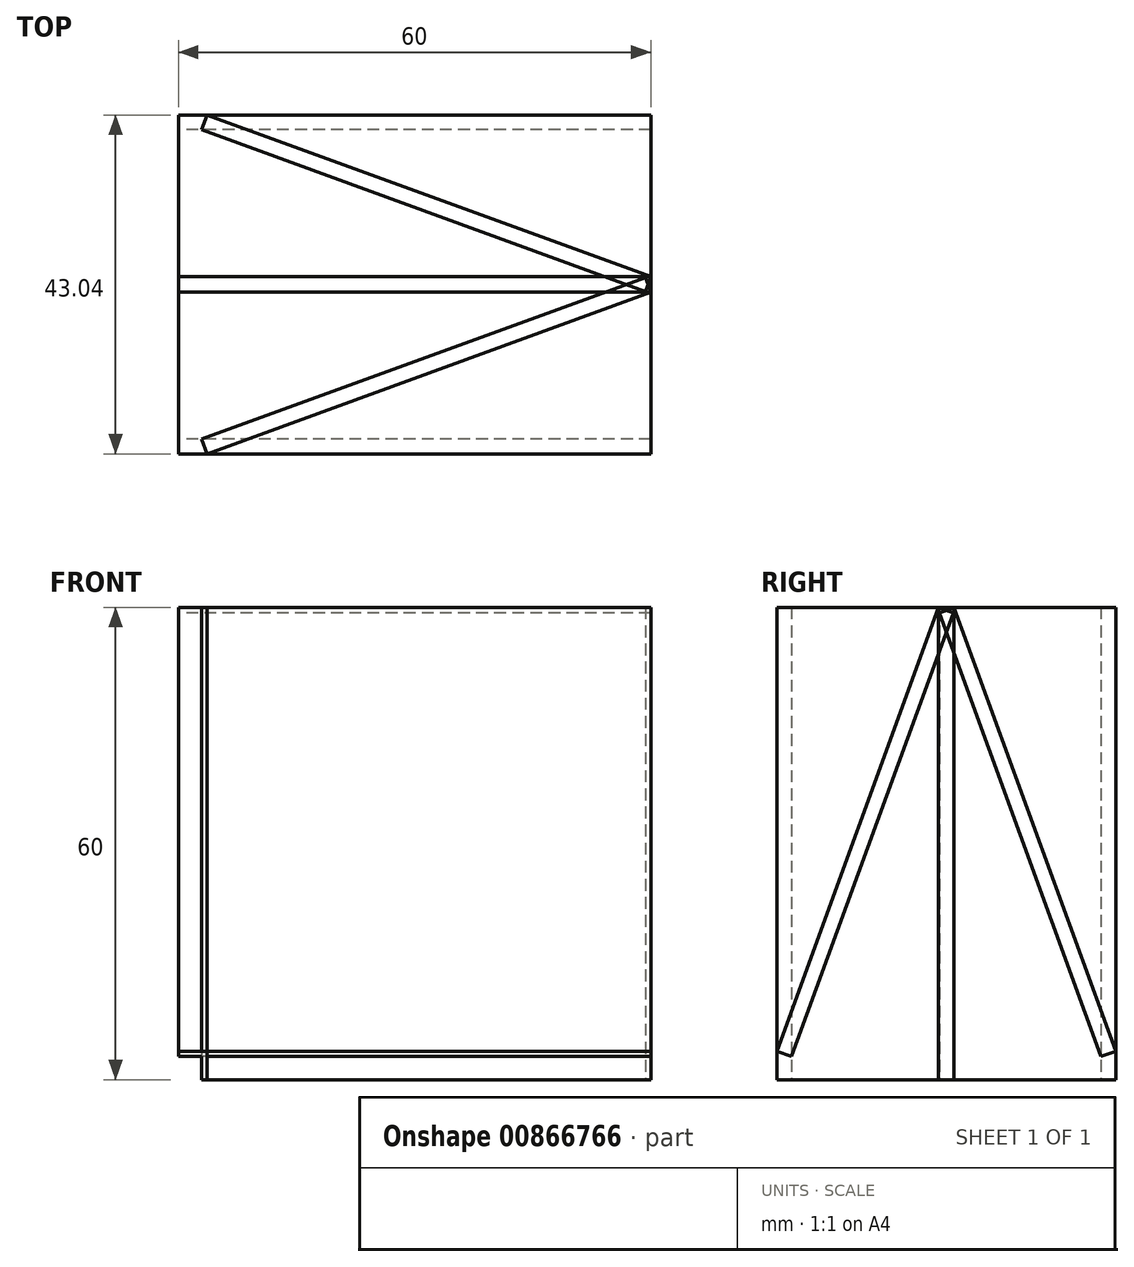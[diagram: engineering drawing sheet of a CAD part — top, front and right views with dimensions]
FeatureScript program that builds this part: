
annotation { "Feature Type Name" : "Feature", "Feature Type Description" : "" }
export const myFeature = defineFeature(function(context is Context, id is Id, definition is map)
    precondition{}
    {
        {
            var Q0;
            Q0=qCreatedBy(makeId("Front.planeOp"),FACE);
            var sketch = newSketch(context, id + "F0", { "sketchPlane" : qUnion([Q0])});
            skLineSegment(sketch, "E0.bottom", {"start": v(0, 0) * mm, "end": v(-60, 0) * mm});
            skLineSegment(sketch, "E0.top", {"start": v(0, -60) * mm, "end": v(-60, -60) * mm});
            skLineSegment(sketch, "E0.left", {"start": v(0, 0) * mm, "end": v(0, -60) * mm});
            skLineSegment(sketch, "E0.right", {"start": v(-60, 0) * mm, "end": v(-60, -60) * mm});
            skSolve(sketch);
        }
        {
            var Q0;
            Q0=makeQuery(id+"F0.imprint","IMPRINT",FACE,{"disambiguationData":[TD([[makeQuery(id+"F0.imprint","IMPRINT",EDGE,{"derivedFrom":sQuery(id+"F0.wireOp",EDGE,"E0.bottom")}),1.0]])]});
            extrude(context, id + "F1", {"entities" : qUnion([Q0]), "depth" : 2 * mm, "offsetDistance" : 25 * mm});
        }
        {
            var Q0;
            Q0=makeQuery(id+"F1.opExtrude","SWEPT_BODY",BODY,{"disambiguationData":[OSD([sQuery(id+"F0.wireOp",EDGE,"E0.bottom"),sQuery(id+"F0.wireOp",EDGE,"E0.top"),sQuery(id+"F0.wireOp",EDGE,"E0.left"),sQuery(id+"F0.wireOp",EDGE,"E0.right")])]});
            var Q1;
            Q1=makeQuery(id+"F1.opExtrude","CAP_EDGE",EDGE,{"disambiguationData":[OSD([sQuery(id+"F0.wireOp",EDGE,"E0.bottom")])],"isStart":false});
            transform(context, id + "F2", {"entities" : qUnion([Q0]), "transformType" : TransformType.ROTATION, "transformAxis" : qUnion([Q1]), "angle" : 20 * degree, "makeCopy" : true});
        }
        {
            var Q0;
            Q0=makeQuery(id+"F1.opExtrude","SWEPT_BODY",BODY,{"disambiguationData":[OSD([sQuery(id+"F0.wireOp",EDGE,"E0.bottom"),sQuery(id+"F0.wireOp",EDGE,"E0.top"),sQuery(id+"F0.wireOp",EDGE,"E0.left"),sQuery(id+"F0.wireOp",EDGE,"E0.right")])]});
            var Q1;
            Q1=makeQuery(id+"F1.opExtrude","CAP_EDGE",EDGE,{"disambiguationData":[OSD([sQuery(id+"F0.wireOp",EDGE,"E0.bottom")])],"isStart":true});
            transform(context, id + "F3", {"entities" : qUnion([Q0]), "transformType" : TransformType.ROTATION, "transformAxis" : qUnion([Q1]), "angle" : 340 * degree, "makeCopy" : true});
        }
        {
            var Q0;
            Q0=makeQuery(id+"F1.opExtrude","SWEPT_BODY",BODY,{"disambiguationData":[OSD([sQuery(id+"F0.wireOp",EDGE,"E0.bottom"),sQuery(id+"F0.wireOp",EDGE,"E0.top"),sQuery(id+"F0.wireOp",EDGE,"E0.left"),sQuery(id+"F0.wireOp",EDGE,"E0.right")])]});
            var Q1;
            Q1=makeQuery(id+"F1.opExtrude","CAP_EDGE",EDGE,{"disambiguationData":[OSD([sQuery(id+"F0.wireOp",EDGE,"E0.left")])],"isStart":true});
            transform(context, id + "F4", {"entities" : qUnion([Q0]), "transformType" : TransformType.ROTATION, "transformAxis" : qUnion([Q1]), "angle" : 20 * degree, "makeCopy" : true});
        }
        {
            var Q0;
            Q0=makeQuery(id+"F1.opExtrude","SWEPT_BODY",BODY,{"disambiguationData":[OSD([sQuery(id+"F0.wireOp",EDGE,"E0.bottom"),sQuery(id+"F0.wireOp",EDGE,"E0.top"),sQuery(id+"F0.wireOp",EDGE,"E0.left"),sQuery(id+"F0.wireOp",EDGE,"E0.right")])]});
            var Q1;
            Q1=makeQuery(id+"F1.opExtrude","CAP_EDGE",EDGE,{"disambiguationData":[OSD([sQuery(id+"F0.wireOp",EDGE,"E0.left")])],"isStart":false});
            transform(context, id + "F5", {"entities" : qUnion([Q0]), "transformType" : TransformType.ROTATION, "transformAxis" : qUnion([Q1]), "angle" : 340 * degree, "makeCopy" : true});
        }
        {
            var Q0;
            Q0=makeQuery(id+"F1.opExtrude","SWEPT_BODY",BODY,{"disambiguationData":[OSD([sQuery(id+"F0.wireOp",EDGE,"E0.bottom"),sQuery(id+"F0.wireOp",EDGE,"E0.top"),sQuery(id+"F0.wireOp",EDGE,"E0.left"),sQuery(id+"F0.wireOp",EDGE,"E0.right")])]});
            deleteBodies(context, id + "F6", {"entities" : qUnion([Q0])});
        }
    });
